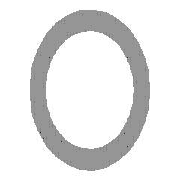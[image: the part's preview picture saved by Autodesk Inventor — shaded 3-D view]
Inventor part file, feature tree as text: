
AUTODESK INVENTOR PART (.ipt)
format: ipt  version: 2021 (Build 250183000, 183)  size: 373,760 bytes
history: native  units: mm (DEFAULTED — no unit token found)
features: other x5, plane x2, sketch x2, sweep x1
ambient origin geometry x8: Origin, YZ Plane, XZ Plane, XY Plane, X Axis, Y Axis, Z Axis, Center Point
bodies: Solid1 (feature_tree)
feature tree (10):
  parser-record x1  (decoder bookkeeping rows leaked as tree rows — omitted from the tree; the rows remain in map.json)
  other  "Driven Length"
  other  "Plano inicial"
  other  "Plano final"
  other  "Trayectoria de barrido"
  plane  "Plano de trabajo de orientación"
  sweep  "Cuerpo"
  sketch  "Sketch3"  dims[d0=26.67mm d1=3.9116mm]
  plane  "Work Plane3"
  sketch  "Sketch4"  dims[d4=-0.0mm d5=1165.819732mm d6=90.0deg d7=1165.819732mm d8=0.0mm d9=0.0mm]
